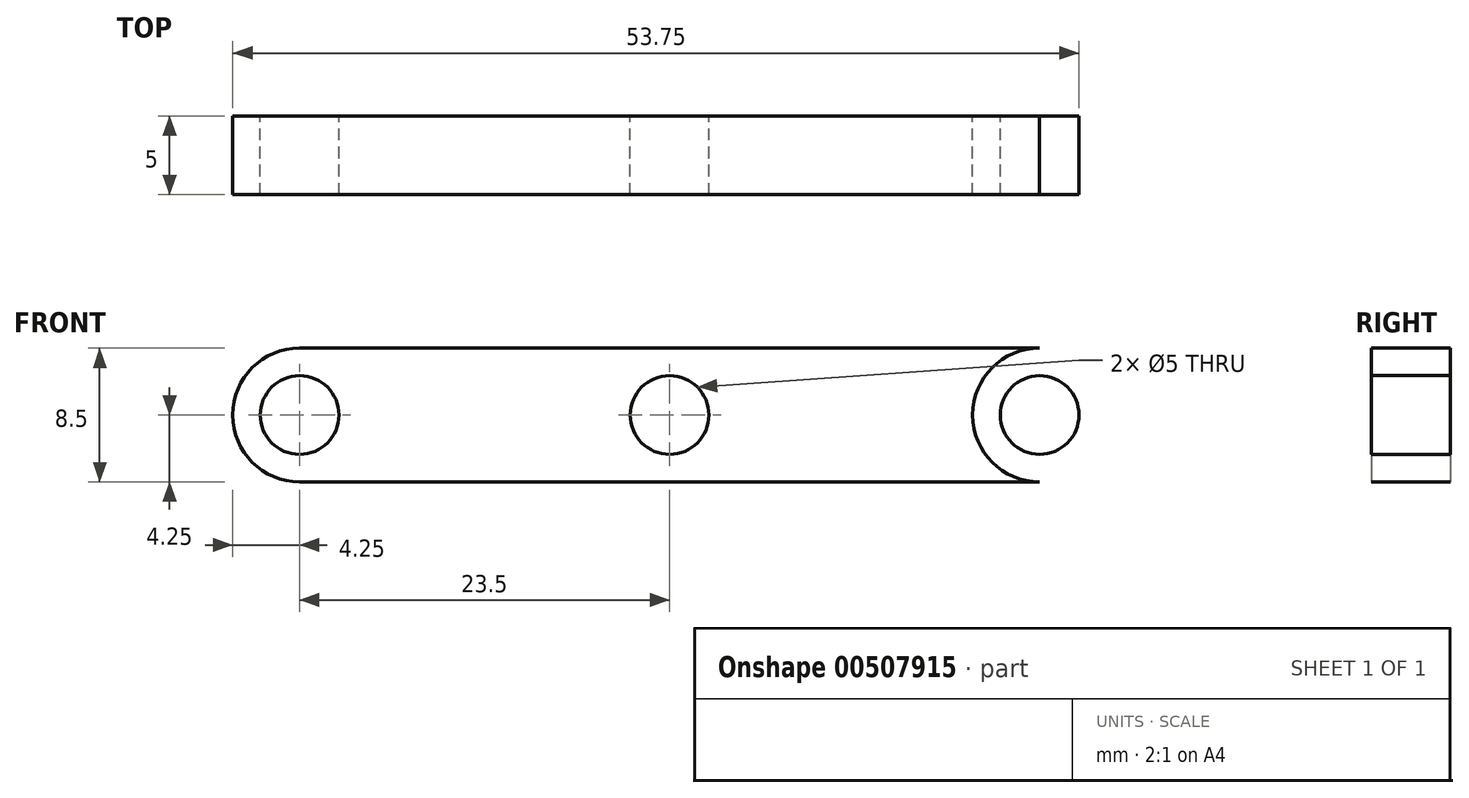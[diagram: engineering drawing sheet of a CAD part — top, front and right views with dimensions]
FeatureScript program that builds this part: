
annotation { "Feature Type Name" : "Feature", "Feature Type Description" : "" }
export const myFeature = defineFeature(function(context is Context, id is Id, definition is map)
    precondition{}
    {
        {
            var Q0;
            Q0=qCreatedBy(makeId("Front.planeOp"),FACE);
            var sketch = newSketch(context, id + "F0", { "sketchPlane" : qUnion([Q0])});
            skLineSegment(sketch, "E0", {"start": v(0, 0) * mm, "end": v(47, 0) * mm, "construction": true});
            skLineSegment(sketch, "E1", {"start": v(23.5, 0) * mm, "end": v(23.5, -22) * mm, "construction": true});
            skCircle(sketch, "E2", {"center": v(0, 0) * mm, "radius": 2.5 * mm});
            skCircle(sketch, "E3", {"center": v(0, 0) * mm, "radius": 4.25 * mm});
            skLineSegment(sketch, "E4", {"start": v(0, -4.25) * mm, "end": v(23.5, -4.25) * mm});
            skLineSegment(sketch, "E5", {"start": v(0, 4.25) * mm, "end": v(23.5, 4.25) * mm});
            skLineSegment(sketch, "E6.MirrorCS", {"start": v(47, -4.25) * mm, "end": v(23.5, -4.25) * mm});
            skLineSegment(sketch, "E7.MirrorCS", {"start": v(47, 4.25) * mm, "end": v(23.5, 4.25) * mm});
            skCircle(sketch, "E8.MirrorC", {"center": v(47, 0) * mm, "radius": 4.25 * mm});
            skCircle(sketch, "E9.MirrorC", {"center": v(47, 0) * mm, "radius": 2.5 * mm});
            skCircle(sketch, "E10", {"center": v(23.5, 0) * mm, "radius": 2.5 * mm});
            skSolve(sketch);
        }
        {
            var Q0;
            Q0=makeQuery(id+"F0.imprint","IMPRINT",FACE,{"disambiguationData":[TD([[makeQuery(id+"F0.imprint","IMPRINT",EDGE,{"derivedFrom":sQuery(id+"F0.wireOp",EDGE,"E2")}),-1.0]])]});
            var Q1;
            {var subQ2=sQuery(id+"F0.wireOp",EDGE,"E4");Q1=makeQuery(id+"F0.imprint","IMPRINT",FACE,{"disambiguationData":[TD([[makeQuery(id+"F0.imprint","IMPRINT",EDGE,{"derivedFrom":subQ2}),1.0]])]});}
            var Q2;
            Q2=makeQuery(id+"F0.imprint","IMPRINT",FACE,{"disambiguationData":[TD([[makeQuery(id+"F0.imprint","IMPRINT",EDGE,{"derivedFrom":sQuery(id+"F0.wireOp",EDGE,"E9.MirrorC")}),1.0]])]});
            extrude(context, id + "F1", {"entities" : qUnion([Q0, Q1, Q2]), "depth" : 5 * mm, "offsetDistance" : 25 * mm});
        }
    });
